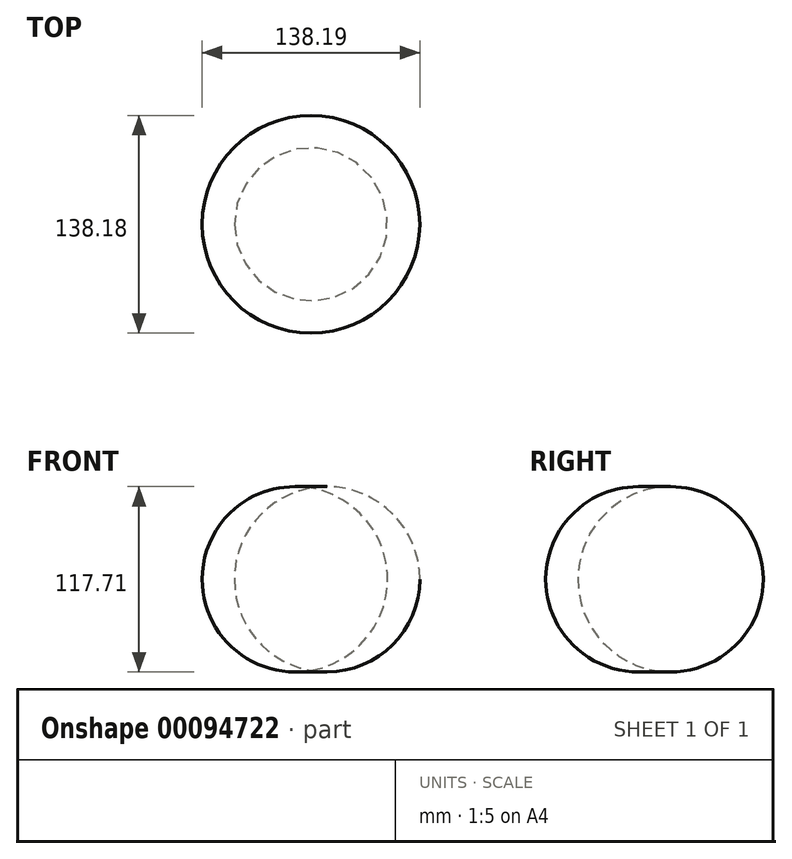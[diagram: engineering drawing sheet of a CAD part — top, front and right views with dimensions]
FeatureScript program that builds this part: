
annotation { "Feature Type Name" : "Feature", "Feature Type Description" : "" }
export const myFeature = defineFeature(function(context is Context, id is Id, definition is map)
    precondition{}
    {
        {
            var Q0;
            Q0=qCreatedBy(makeId("Front.planeOp"),FACE);
            var sketch = newSketch(context, id + "F0", { "sketchPlane" : qUnion([Q0])});
            skLineSegment(sketch, "E0", {"start": v(-50.06, 57.36) * mm, "end": v(-50.06, -58.55) * mm});
            skArc(sketch, "E1", {"start": v(-50.06, -58.55) * mm, "mid": v(-1.44, -0.6) * mm, "end": v(-50.06, 57.36) * mm});
            skSolve(sketch);
        }
        {
            var Q0;
            Q0=makeQuery(id+"F0.imprint","IMPRINT",FACE,{"disambiguationData":[TD([[makeQuery(id+"F0.imprint","IMPRINT",EDGE,{"derivedFrom":sQuery(id+"F0.wireOp",EDGE,"E0")}),1.0]])]});
            var Q1;
            Q1=sQuery(id+"F0.wireOp",EDGE,"E0");
            revolve(context, id + "F1", {"entities" : qUnion([Q0]), "axis" : qUnion([Q1]), "revolveType" : RevolveType.FULL});
        }
    });
